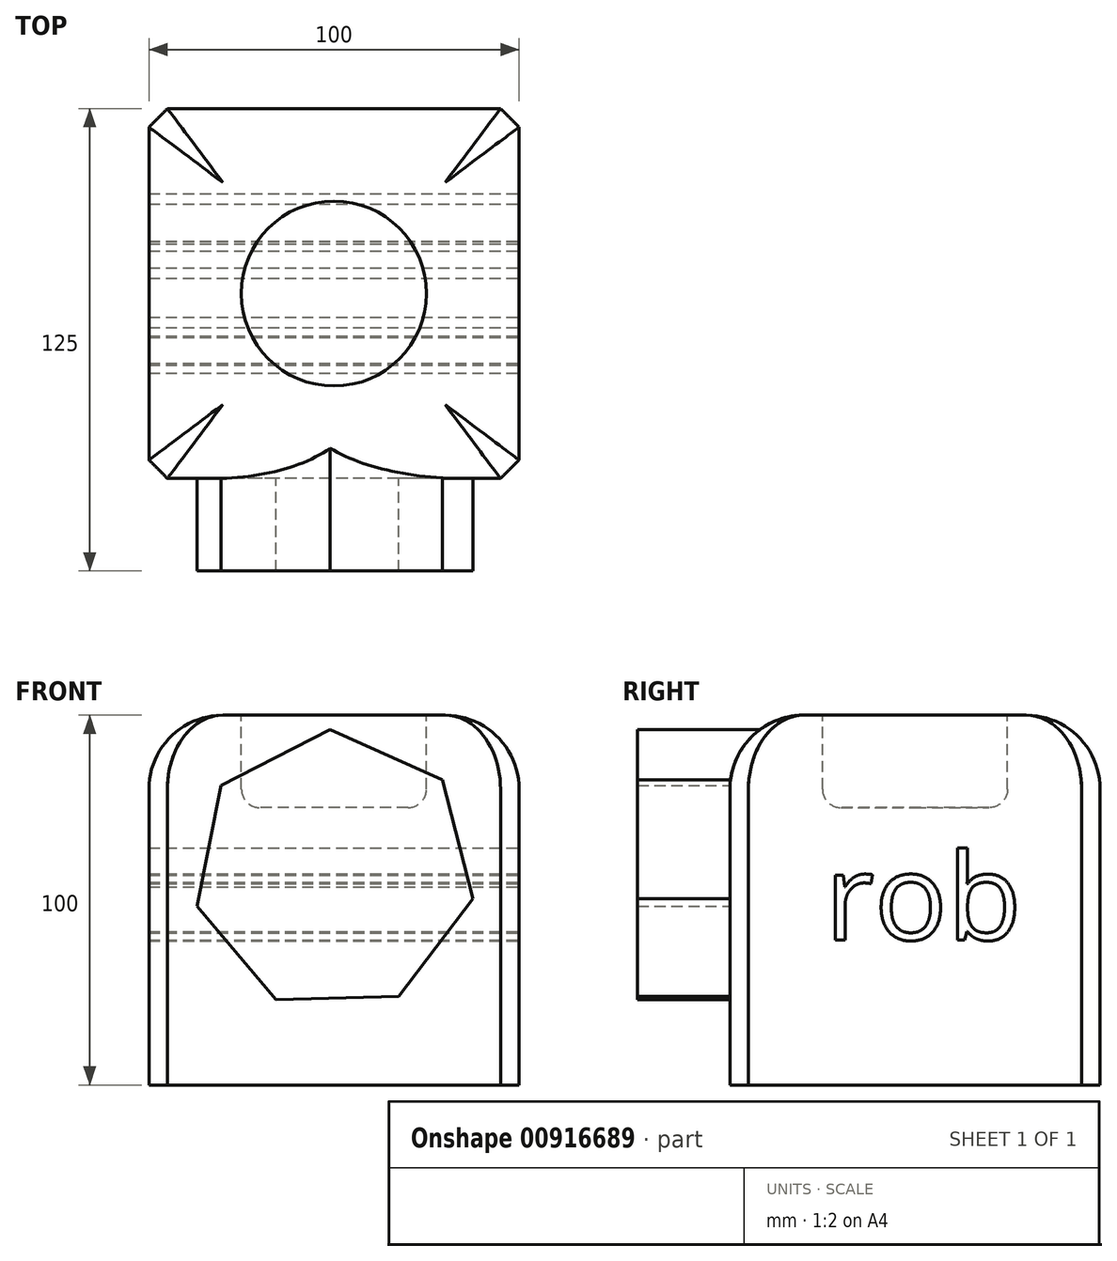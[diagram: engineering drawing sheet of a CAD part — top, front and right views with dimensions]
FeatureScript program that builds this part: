
annotation { "Feature Type Name" : "Feature", "Feature Type Description" : "" }
export const myFeature = defineFeature(function(context is Context, id is Id, definition is map)
    precondition{}
    {
        {
            var Q0;
            Q0=qCreatedBy(makeId("Top.planeOp"),FACE);
            var sketch = newSketch(context, id + "F0", { "sketchPlane" : qUnion([Q0])});
            skLineSegment(sketch, "E0.bottom", {"start": v(50, -50) * mm, "end": v(-50, -50) * mm});
            skLineSegment(sketch, "E0.top", {"start": v(50, 50) * mm, "end": v(-50, 50) * mm});
            skLineSegment(sketch, "E0.left", {"start": v(50, -50) * mm, "end": v(50, 50) * mm});
            skLineSegment(sketch, "E0.right", {"start": v(-50, -50) * mm, "end": v(-50, 50) * mm});
            skPoint(sketch, "E0.middle", {"position": v(0, 0) * mm});
            skSolve(sketch);
        }
        {
            var Q0;
            Q0=makeQuery(id+"F0.imprint","IMPRINT",FACE,{"disambiguationData":[TD([[makeQuery(id+"F0.imprint","IMPRINT",EDGE,{"derivedFrom":sQuery(id+"F0.wireOp",EDGE,"E0.bottom")}),-1.0]])]});
            extrude(context, id + "F1", {"entities" : qUnion([Q0]), "depth" : 100 * mm, "offsetDistance" : 25 * mm});
        }
        {
            var Q0;
            Q0=makeQuery(id+"F1.opExtrude","CAP_FACE",FACE,{"disambiguationData":[OSD([sQuery(id+"F0.wireOp",EDGE,"E0.bottom"),sQuery(id+"F0.wireOp",EDGE,"E0.top"),sQuery(id+"F0.wireOp",EDGE,"E0.left"),sQuery(id+"F0.wireOp",EDGE,"E0.right")])],"isStart":false});
            var sketch = newSketch(context, id + "F2", { "sketchPlane" : qUnion([Q0])});
            skCircle(sketch, "E1", {"center": v(0, 0) * mm, "radius": 25 * mm});
            skSolve(sketch);
        }
        {
            var Q0;
            Q0=makeQuery(id+"F2.imprint","IMPRINT",FACE,{"disambiguationData":[TD([[makeQuery(id+"F2.imprint","IMPRINT",EDGE,{"derivedFrom":sQuery(id+"F2.wireOp",EDGE,"E1")}),1.0]])]});
            extrude(context, id + "F3", {"entities" : qUnion([Q0]), "operationType" : NewBodyOperationType.REMOVE, "oppositeDirection" : true, "depth" : 25 * mm, "offsetDistance" : 25 * mm});
        }
        {
            var Q0;
            Q0=makeQuery(id+"F1.opExtrude","SWEPT_FACE",FACE,{"disambiguationData":[OSD([sQuery(id+"F0.wireOp",EDGE,"E0.bottom")])]});
            var sketch = newSketch(context, id + "F4", { "sketchPlane" : qUnion([Q0])});
            skCircle(sketch, "E2.cCircle", {"center": v(0, 57.9) * mm, "radius": 34.45 * mm, "construction": true});
            skLineSegment(sketch, "E2.0", {"start": v(29.24, 82.54) * mm, "end": v(37.5, 50.4) * mm});
            skLineSegment(sketch, "E2.1", {"start": v(37.5, 50.4) * mm, "end": v(17.52, 23.91) * mm});
            skLineSegment(sketch, "E2.2", {"start": v(17.52, 23.91) * mm, "end": v(-15.65, 23.01) * mm});
            skLineSegment(sketch, "E2.3", {"start": v(-15.65, 23.01) * mm, "end": v(-37.03, 48.38) * mm});
            skLineSegment(sketch, "E2.4", {"start": v(-37.03, 48.38) * mm, "end": v(-30.53, 80.92) * mm});
            skLineSegment(sketch, "E2.5", {"start": v(-30.53, 80.92) * mm, "end": v(-1.04, 96.12) * mm});
            skLineSegment(sketch, "E2.6", {"start": v(-1.04, 96.12) * mm, "end": v(29.24, 82.54) * mm});
            skPoint(sketch, "E2.0.midPoint", {"position": v(33.37, 66.47) * mm});
            skSolve(sketch);
        }
        {
            var Q0;
            Q0=makeQuery(id+"F4.imprint","IMPRINT",FACE,{"disambiguationData":[TD([[makeQuery(id+"F4.imprint","IMPRINT",EDGE,{"derivedFrom":sQuery(id+"F4.wireOp",EDGE,"E2.0")}),-1.0]])]});
            extrude(context, id + "F5", {"entities" : qUnion([Q0]), "operationType" : NewBodyOperationType.ADD, "depth" : 25 * mm, "offsetDistance" : 25 * mm});
        }
        {
            var Q0;
            Q0=makeQuery(id+"F1.opExtrude","SWEPT_FACE",FACE,{"disambiguationData":[OSD([sQuery(id+"F0.wireOp",EDGE,"E0.left")])]});
            var sketch = newSketch(context, id + "F6", { "sketchPlane" : qUnion([Q0])});
            skSolve(sketch);
        }
        {
            var Q0;
            {var subQ0=sQuery(id+"F0.wireOp",EDGE,"E0.left");Q0=makeQuery(id+"F6.imprint","IMPRINT",FACE,{"disambiguationData":[TD([[makeQuery(id+"F6.imprint","IMPRINT",EDGE,{"derivedFrom":makeQuery(id+"F1.opExtrude","CAP_EDGE",EDGE,{"disambiguationData":[OSD([subQ0])],"isStart":true})}),1.0]])]});}
            var sketch = newSketch(context, id + "F7", { "sketchPlane" : qUnion([Q0])});
            skText(sketch, "E3", { "text": "rob", "fontName": "OpenSans-Regular.ttf"});
            const initialGuessF7  = {"E3": [-0.02433, 0.03924, 1, 0, 0.02352]};
            skSetInitialGuess(sketch, initialGuessF7);
            skSolve(sketch);
        }
        {
            var Q0;
            Q0 = qSketchRegion(id + "F7", true);
            extrude(context, id + "F8", {"entities" : qUnion([Q0]), "operationType" : NewBodyOperationType.REMOVE, "oppositeDirection" : true, "depth" : 100 * mm, "offsetDistance" : 25 * mm});
        }
        {
            var Q0;
            Q0=makeQuery(id+"F1.opExtrude","CAP_EDGE",EDGE,{"disambiguationData":[OSD([sQuery(id+"F0.wireOp",EDGE,"E0.bottom")])],"isStart":false});
            var Q1;
            Q1=makeQuery(id+"F1.opExtrude","CAP_EDGE",EDGE,{"disambiguationData":[OSD([sQuery(id+"F0.wireOp",EDGE,"E0.left")])],"isStart":false});
            var Q2;
            Q2=makeQuery(id+"F1.opExtrude","CAP_EDGE",EDGE,{"disambiguationData":[OSD([sQuery(id+"F0.wireOp",EDGE,"E0.top")])],"isStart":false});
            var Q3;
            Q3=makeQuery(id+"F1.opExtrude","CAP_EDGE",EDGE,{"disambiguationData":[OSD([sQuery(id+"F0.wireOp",EDGE,"E0.right")])],"isStart":false});
            fillet(context, id + "F9", {"entities" : qUnion([Q0, Q1, Q2, Q3]), "radius" : 20 * mm, "tangentPropagation" : true, "allowEdgeOverflow" : false});
        }
        {
            var Q0;
            Q0=makeQuery(id+"F3.boolean.opBoolean","COPY",EDGE,{"derivedFrom":makeQuery(id+"F3.opExtrude","CAP_EDGE",EDGE,{"disambiguationData":[OSD([sQuery(id+"F2.wireOp",EDGE,"E1")])],"isStart":false})});
            var Q1;
            Q1=makeQuery(id+"F3.boolean.opBoolean","COPY",EDGE,{"derivedFrom":makeQuery(id+"F3.opExtrude","CAP_EDGE",EDGE,{"disambiguationData":[OSD([sQuery(id+"F2.wireOp",EDGE,"E1")])],"isStart":true})});
            fillet(context, id + "F10", {"entities" : qUnion([Q0, Q1]), "radius" : 5 * mm, "tangentPropagation" : true, "allowEdgeOverflow" : false});
        }
        {
            var Q0;
            Q0=makeQuery(id+"F1.opExtrude","SWEPT_EDGE",EDGE,{"disambiguationData":[OSD([sQuery(id+"F0.wireOp",EDGE,"E0.top"),sQuery(id+"F0.wireOp",EDGE,"E0.left")])]});
            var Q1;
            Q1=makeQuery(id+"F1.opExtrude","SWEPT_EDGE",EDGE,{"disambiguationData":[OSD([sQuery(id+"F0.wireOp",EDGE,"E0.bottom"),sQuery(id+"F0.wireOp",EDGE,"E0.left")])]});
            var Q2;
            Q2=makeQuery(id+"F1.opExtrude","SWEPT_EDGE",EDGE,{"disambiguationData":[OSD([sQuery(id+"F0.wireOp",EDGE,"E0.bottom"),sQuery(id+"F0.wireOp",EDGE,"E0.right")])]});
            var Q3;
            Q3=makeQuery(id+"F1.opExtrude","SWEPT_EDGE",EDGE,{"disambiguationData":[OSD([sQuery(id+"F0.wireOp",EDGE,"E0.top"),sQuery(id+"F0.wireOp",EDGE,"E0.right")])]});
            chamfer(context, id + "F11", {"entities" : qUnion([Q0, Q1, Q2, Q3]), "width" : 5 * mm, "tangentPropagation" : true});
        }
    });
